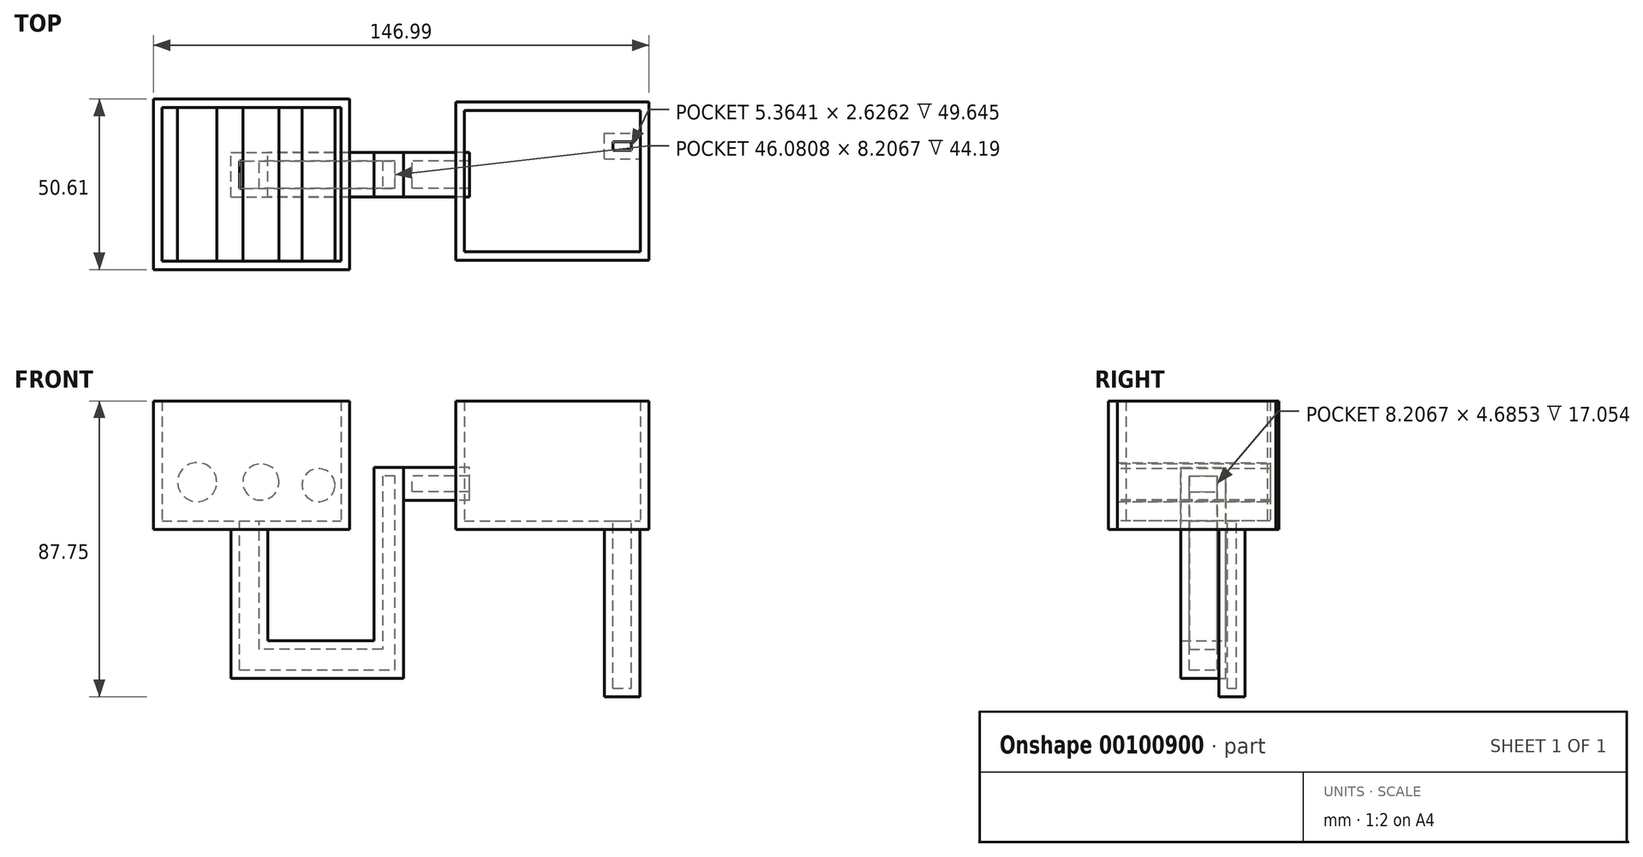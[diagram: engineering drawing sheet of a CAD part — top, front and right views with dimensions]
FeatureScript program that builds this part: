
annotation { "Feature Type Name" : "Feature", "Feature Type Description" : "" }
export const myFeature = defineFeature(function(context is Context, id is Id, definition is map)
    precondition{}
    {
        {
            var Q0;
            Q0=qCreatedBy(makeId("Top.planeOp"),FACE);
            var sketch = newSketch(context, id + "F0", { "sketchPlane" : qUnion([Q0])});
            skLineSegment(sketch, "E0.bottom", {"start": v(-68.34, 23.94) * mm, "end": v(-10.15, 23.94) * mm});
            skLineSegment(sketch, "E0.top", {"start": v(-68.34, -26.67) * mm, "end": v(-10.15, -26.67) * mm});
            skLineSegment(sketch, "E0.left", {"start": v(-68.34, 23.94) * mm, "end": v(-68.34, -26.67) * mm});
            skLineSegment(sketch, "E0.right", {"start": v(-10.15, 23.94) * mm, "end": v(-10.15, -26.67) * mm});
            skSolve(sketch);
        }
        {
            var Q0;
            Q0=makeQuery(id+"F0.imprint","IMPRINT",FACE,{"disambiguationData":[TD([[makeQuery(id+"F0.imprint","IMPRINT",EDGE,{"derivedFrom":sQuery(id+"F0.wireOp",EDGE,"E0.bottom")}),-1.0]])]});
            extrude(context, id + "F1", {"entities" : qUnion([Q0]), "depth" : 38.1 * mm});
        }
        {
            var Q0;
            Q0=qCreatedBy(makeId("Top.planeOp"),FACE);
            var sketch = newSketch(context, id + "F2", { "sketchPlane" : qUnion([Q0])});
            skLineSegment(sketch, "E1.bottom", {"start": v(21.37, 23.03) * mm, "end": v(78.65, 23.03) * mm});
            skLineSegment(sketch, "E1.top", {"start": v(21.37, -23.94) * mm, "end": v(78.65, -23.94) * mm});
            skLineSegment(sketch, "E1.left", {"start": v(21.37, 23.03) * mm, "end": v(21.37, -23.94) * mm});
            skLineSegment(sketch, "E1.right", {"start": v(78.65, 23.03) * mm, "end": v(78.65, -23.94) * mm});
            skSolve(sketch);
        }
        {
            var Q0;
            Q0=makeQuery(id+"F2.imprint","IMPRINT",FACE,{"disambiguationData":[TD([[makeQuery(id+"F2.imprint","IMPRINT",EDGE,{"derivedFrom":sQuery(id+"F2.wireOp",EDGE,"E1.bottom")}),-1.0]])]});
            extrude(context, id + "F3", {"entities" : qUnion([Q0]), "depth" : 38.1 * mm});
        }
        {
            var Q0;
            Q0=makeQuery(id+"F3.opExtrude","CAP_FACE",FACE,{"disambiguationData":[OSD([sQuery(id+"F2.wireOp",EDGE,"E1.bottom"),sQuery(id+"F2.wireOp",EDGE,"E1.top"),sQuery(id+"F2.wireOp",EDGE,"E1.left"),sQuery(id+"F2.wireOp",EDGE,"E1.right")])],"isStart":true});
            var sketch = newSketch(context, id + "F4", { "sketchPlane" : qUnion([Q0])});
            skLineSegment(sketch, "E2.bottom", {"start": v(21.37, -23.03) * mm, "end": v(78.65, -23.03) * mm});
            skLineSegment(sketch, "E2.top", {"start": v(21.37, 23.94) * mm, "end": v(78.65, 23.94) * mm});
            skLineSegment(sketch, "E2.left", {"start": v(21.37, -23.03) * mm, "end": v(21.37, 23.94) * mm});
            skLineSegment(sketch, "E2.right", {"start": v(78.65, -23.03) * mm, "end": v(78.65, 23.94) * mm});
            skSolve(sketch);
        }
        {
            var Q0;
            Q0=makeQuery(id+"F1.opExtrude","CAP_FACE",FACE,{"disambiguationData":[OSD([sQuery(id+"F0.wireOp",EDGE,"E0.bottom"),sQuery(id+"F0.wireOp",EDGE,"E0.top"),sQuery(id+"F0.wireOp",EDGE,"E0.left"),sQuery(id+"F0.wireOp",EDGE,"E0.right")])],"isStart":true});
            var sketch = newSketch(context, id + "F5", { "sketchPlane" : qUnion([Q0])});
            skLineSegment(sketch, "E3.bottom", {"start": v(-45.3, 5.14) * mm, "end": v(-34.39, 5.14) * mm});
            skLineSegment(sketch, "E3.top", {"start": v(-45.3, -8.14) * mm, "end": v(-34.39, -8.14) * mm});
            skLineSegment(sketch, "E3.left", {"start": v(-45.3, 5.14) * mm, "end": v(-45.3, -8.14) * mm});
            skLineSegment(sketch, "E3.right", {"start": v(-34.39, 5.14) * mm, "end": v(-34.39, -8.14) * mm});
            skSolve(sketch);
        }
        {
            var Q0;
            Q0=makeQuery(id+"F5.imprint","IMPRINT",FACE,{"disambiguationData":[TD([[makeQuery(id+"F5.imprint","IMPRINT",EDGE,{"derivedFrom":sQuery(id+"F5.wireOp",EDGE,"E3.bottom")}),-1.0]])]});
            extrude(context, id + "F6", {"entities" : qUnion([Q0]), "operationType" : NewBodyOperationType.ADD, "depth" : 44.2 * mm});
        }
        {
            var Q0;
            Q0=makeQuery(id+"F6.opExtrude","SWEPT_FACE",FACE,{"disambiguationData":[OSD([sQuery(id+"F5.wireOp",EDGE,"E3.right")])]});
            var sketch = newSketch(context, id + "F7", { "sketchPlane" : qUnion([Q0])});
            skLineSegment(sketch, "E4.bottom", {"start": v(-5.14, -33.03) * mm, "end": v(8.14, -33.03) * mm});
            skLineSegment(sketch, "E4.top", {"start": v(-5.14, -44.2) * mm, "end": v(8.14, -44.2) * mm});
            skLineSegment(sketch, "E4.left", {"start": v(-5.14, -33.03) * mm, "end": v(-5.14, -44.2) * mm});
            skLineSegment(sketch, "E4.right", {"start": v(8.14, -33.03) * mm, "end": v(8.14, -44.2) * mm});
            skSolve(sketch);
        }
        {
            var Q0;
            Q0=makeQuery(id+"F7.imprint","IMPRINT",FACE,{"disambiguationData":[TD([[makeQuery(id+"F7.imprint","IMPRINT",EDGE,{"derivedFrom":sQuery(id+"F7.wireOp",EDGE,"E4.bottom")}),-1.0]])]});
            extrude(context, id + "F8", {"entities" : qUnion([Q0]), "operationType" : NewBodyOperationType.ADD, "depth" : 40.25 * mm});
        }
        {
            var Q0;
            Q0=makeQuery(id+"F8.opExtrude","SWEPT_FACE",FACE,{"disambiguationData":[OSD([sQuery(id+"F7.wireOp",EDGE,"E4.bottom")])]});
            var sketch = newSketch(context, id + "F9", { "sketchPlane" : qUnion([Q0])});
            skLineSegment(sketch, "E5.bottom", {"start": v(-2.87, 8.14) * mm, "end": v(5.86, 8.14) * mm});
            skLineSegment(sketch, "E5.top", {"start": v(-2.87, -5.14) * mm, "end": v(5.86, -5.14) * mm});
            skLineSegment(sketch, "E5.left", {"start": v(-2.87, 8.14) * mm, "end": v(-2.87, -5.14) * mm});
            skLineSegment(sketch, "E5.right", {"start": v(5.86, 8.14) * mm, "end": v(5.86, -5.14) * mm});
            skSolve(sketch);
        }
        {
            var Q0;
            Q0=makeQuery(id+"F9.imprint","IMPRINT",FACE,{"disambiguationData":[TD([[makeQuery(id+"F9.imprint","IMPRINT",EDGE,{"derivedFrom":sQuery(id+"F9.wireOp",EDGE,"E5.bottom")}),1.0]])]});
            extrude(context, id + "F10", {"entities" : qUnion([Q0]), "operationType" : NewBodyOperationType.ADD, "depth" : 51.46 * mm});
        }
        {
            var Q0;
            Q0=makeQuery(id+"F10.boolean.opBoolean","MERGE",FACE,{"derivedFrom":[makeQuery(id+"F8.opExtrude","CAP_FACE",FACE,{"disambiguationData":[OSD([sQuery(id+"F7.wireOp",EDGE,"E4.bottom"),sQuery(id+"F7.wireOp",EDGE,"E4.top"),sQuery(id+"F7.wireOp",EDGE,"E4.left"),sQuery(id+"F7.wireOp",EDGE,"E4.right")])],"isStart":false}),makeQuery(id+"F10.opExtrude","SWEPT_FACE",FACE,{"disambiguationData":[OSD([sQuery(id+"F9.wireOp",EDGE,"E5.right")])]})]});
            var sketch = newSketch(context, id + "F11", { "sketchPlane" : qUnion([Q0])});
            skLineSegment(sketch, "E6.bottom", {"start": v(-5.14, 18.43) * mm, "end": v(8.14, 18.43) * mm});
            skLineSegment(sketch, "E6.top", {"start": v(-5.14, 8.66) * mm, "end": v(8.14, 8.66) * mm});
            skLineSegment(sketch, "E6.left", {"start": v(-5.14, 18.43) * mm, "end": v(-5.14, 8.66) * mm});
            skLineSegment(sketch, "E6.right", {"start": v(8.14, 18.43) * mm, "end": v(8.14, 8.66) * mm});
            skSolve(sketch);
        }
        {
            var Q0;
            Q0=makeQuery(id+"F4.imprint","IMPRINT",FACE,{"disambiguationData":[TD([[makeQuery(id+"F4.imprint","IMPRINT",EDGE,{"derivedFrom":sQuery(id+"F4.wireOp",EDGE,"E2.bottom")}),1.0]])]});
            var sketch = newSketch(context, id + "F12", { "sketchPlane" : qUnion([Q0])});
            skLineSegment(sketch, "E7.bottom", {"start": v(65.5, -6.17) * mm, "end": v(75.94, -6.17) * mm});
            skLineSegment(sketch, "E7.top", {"start": v(65.5, -13.88) * mm, "end": v(75.94, -13.88) * mm});
            skLineSegment(sketch, "E7.left", {"start": v(65.5, -6.17) * mm, "end": v(65.5, -13.88) * mm});
            skLineSegment(sketch, "E7.right", {"start": v(75.94, -6.17) * mm, "end": v(75.94, -13.88) * mm});
            skSolve(sketch);
        }
        {
            var Q0;
            Q0=makeQuery(id+"F12.imprint","IMPRINT",FACE,{"disambiguationData":[TD([[makeQuery(id+"F12.imprint","IMPRINT",EDGE,{"derivedFrom":sQuery(id+"F12.wireOp",EDGE,"E7.bottom")}),-1.0]])]});
            extrude(context, id + "F13", {"entities" : qUnion([Q0]), "operationType" : NewBodyOperationType.ADD, "depth" : 49.65 * mm});
        }
        {
            var Q0;
            Q0=makeQuery(id+"F1.opExtrude","CAP_FACE",FACE,{"disambiguationData":[OSD([sQuery(id+"F0.wireOp",EDGE,"E0.bottom"),sQuery(id+"F0.wireOp",EDGE,"E0.top"),sQuery(id+"F0.wireOp",EDGE,"E0.left"),sQuery(id+"F0.wireOp",EDGE,"E0.right")])],"isStart":false});
            shell(context, id + "F14", {"entities" : qUnion([Q0]), "thickness" : 2.54 * mm});
        }
        {
            var Q0;
            Q0=makeQuery(id+"F3.opExtrude","CAP_FACE",FACE,{"disambiguationData":[OSD([sQuery(id+"F2.wireOp",EDGE,"E1.bottom"),sQuery(id+"F2.wireOp",EDGE,"E1.top"),sQuery(id+"F2.wireOp",EDGE,"E1.left"),sQuery(id+"F2.wireOp",EDGE,"E1.right")])],"isStart":false});
            shell(context, id + "F15", {"entities" : qUnion([Q0]), "thickness" : 2.54 * mm});
        }
        {
            var Q0;
            Q0 = qSketchRegion(id + "F11", true);
            extrude(context, id + "F16", {"entities" : qUnion([Q0]), "depth" : 19.6 * mm});
        }
        {
            var Q0;
            Q0=makeQuery(id+"F16.opExtrude","CAP_FACE",FACE,{"disambiguationData":[OSD([sQuery(id+"F11.wireOp",EDGE,"E6.bottom"),sQuery(id+"F11.wireOp",EDGE,"E6.top"),sQuery(id+"F11.wireOp",EDGE,"E6.left"),sQuery(id+"F11.wireOp",EDGE,"E6.right")])],"isStart":false});
            shell(context, id + "F17", {"entities" : qUnion([Q0]), "thickness" : 2.54 * mm});
        }
        {
            var Q0;
            Q0=makeQuery(id+"F14.opShell","OFFSET_FACE",FACE,{"disambiguationData":[OSD([sQuery(id+"F0.wireOp",EDGE,"E0.top")])]});
            var sketch = newSketch(context, id + "F18", { "sketchPlane" : qUnion([Q0])});
            skCircle(sketch, "E8", {"center": v(19.34, 13.14) * mm, "radius": 4.9 * mm});
            skSolve(sketch);
        }
        {
            var Q0;
            Q0=makeQuery(id+"F18.imprint","IMPRINT",FACE,{"disambiguationData":[TD([[makeQuery(id+"F18.imprint","IMPRINT",EDGE,{"derivedFrom":sQuery(id+"F18.wireOp",EDGE,"E8")}),1.0]])]});
            extrude(context, id + "F19", {"entities" : qUnion([Q0]), "operationType" : NewBodyOperationType.ADD, "depth" : 46.88 * mm});
        }
        {
            var Q0;
            Q0=makeQuery(id+"F14.opShell","OFFSET_FACE",FACE,{"disambiguationData":[OSD([sQuery(id+"F0.wireOp",EDGE,"E0.top")])]});
            var sketch = newSketch(context, id + "F20", { "sketchPlane" : qUnion([Q0])});
            skCircle(sketch, "E9", {"center": v(36.42, 14.06) * mm, "radius": 5.38 * mm});
            skSolve(sketch);
        }
        {
            var Q0;
            Q0=makeQuery(id+"F20.imprint","IMPRINT",FACE,{"disambiguationData":[TD([[makeQuery(id+"F20.imprint","IMPRINT",EDGE,{"derivedFrom":sQuery(id+"F20.wireOp",EDGE,"E9")}),1.0]])]});
            extrude(context, id + "F21", {"entities" : qUnion([Q0]), "operationType" : NewBodyOperationType.ADD, "depth" : 47.43 * mm});
        }
        {
            var Q0;
            Q0=makeQuery(id+"F14.opShell","OFFSET_FACE",FACE,{"disambiguationData":[OSD([sQuery(id+"F0.wireOp",EDGE,"E0.bottom")])]});
            var sketch = newSketch(context, id + "F22", { "sketchPlane" : qUnion([Q0])});
            skCircle(sketch, "E10", {"center": v(-55.33, 14.05) * mm, "radius": 5.79 * mm});
            skSolve(sketch);
        }
        {
            var Q0;
            Q0=makeQuery(id+"F22.imprint","IMPRINT",FACE,{"disambiguationData":[TD([[makeQuery(id+"F22.imprint","IMPRINT",EDGE,{"derivedFrom":sQuery(id+"F22.wireOp",EDGE,"E10")}),1.0]])]});
            extrude(context, id + "F23", {"entities" : qUnion([Q0]), "operationType" : NewBodyOperationType.ADD, "depth" : 47 * mm});
        }
    });
